# Revit family: ITK Органайзер кабельное кольцо 80х80мм
name_source: partatom
category: Обобщенные модели
revit_build: Autodesk Revit 2016 (Build: 20160314_0715(x64)
units: mm (PartAtom-declared; Revit-internal decimal feet)

## family parameters
Всегда вертикально = Да
Может служить основой для арматурных стержней = Нет
На основе рабочей плоскости = Нет
Общий = Нет
При загрузке вырезать с полостями = Нет
Размер круглого соединителя = Использовать диаметр
Тип детали = Нормальный
Точка расчета площади = Нет

## types (1)
- CR35-8080
    ADSK_Группирование = I. ЩИТЫ И ПУЛЬТЫ
    ADSK_Единица измерения = шт
    ADSK_Завод-изготовитель = IEK
    ADSK_Марка = CR35-8080
    ADSK_Масса = 0
    ADSK_Наименование = ITK Органайзерр кабельное кольцо 80х80мм, серый
    ADSK_Наименование краткое = CR35-8080
    URL = http://www.itk-group.ru
    Высота = 80 мм
    Глубина = 20 мм
    Изготовитель = ITK
    Материал = Окраска - RAL 7035
    Описание = Кабельные органайзеры, кольца и скобы ITK предназначены для организации кабеля и кабельных пучков в шкафах и стойках, обеспечивают их поддержку, гарантируют необходимый радиус изгиба коммутационных шнуров и кабеля при подведении их к оборудованию. При использовании кабельных организаторов и колец существенно снижается вероятность появления перегибов и изломов кабелей.

Кабельные кольца могут устанавливаться в любом месте шкафа, как на 19-дюймовые монтажные профили с фронтальной стороны или сбоку, так и на горизонтальные боковые профили, обеспечивая горизонтальную и вертикальную организацию кабеля. Монтаж осуществляется с помощью крепежа винт-шайба-гайка.
Совместимы со всеми 19-дюймовыми шкафами и стойками ITK.
Обладают современным привлекательным дизайном и продуманной конструкцией.
Удобны в монтаже и эксплуатации.
Соответствие международным стандартам ISO9001, IEC 297, ISO/IEC 11801. 
Сертифицированы по ГОСТ Р.
Все аксессуары идут с крепежом.
Возможно исполнение в двух цветах: серый (RAL7035) и черный (RAL9005).
Всегда в наличии на складе.
Гарантия на все аксессуары до 2-х лет.
    Совместимость = Серия Linea S, N, W,F,O
